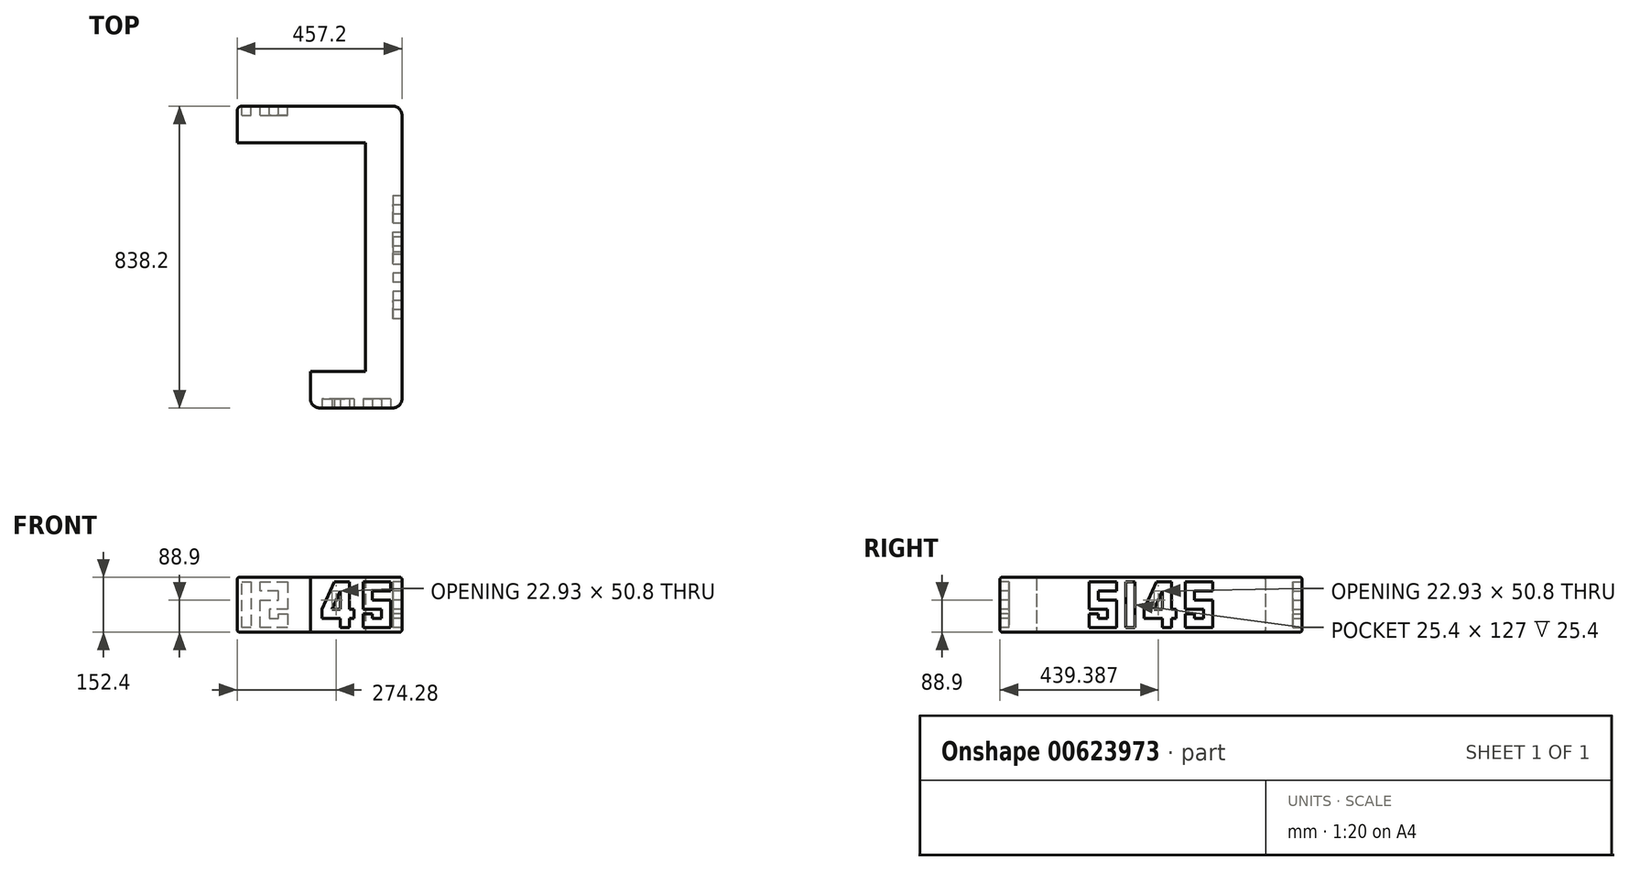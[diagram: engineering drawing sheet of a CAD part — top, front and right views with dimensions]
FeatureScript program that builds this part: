
annotation { "Feature Type Name" : "Feature", "Feature Type Description" : "" }
export const myFeature = defineFeature(function(context is Context, id is Id, definition is map)
    precondition{}
    {
        {
            var Q0;
            Q0=qCreatedBy(makeId("Top.planeOp"),FACE);
            var sketch = newSketch(context, id + "F0", { "sketchPlane" : qUnion([Q0])});
            skLineSegment(sketch, "E0", {"start": v(-261.38, 279.44) * mm, "end": v(94.22, 279.44) * mm});
            skLineSegment(sketch, "E1", {"start": v(94.22, 279.44) * mm, "end": v(94.22, -355.56) * mm});
            skLineSegment(sketch, "E2", {"start": v(94.22, -355.56) * mm, "end": v(-58.18, -355.56) * mm});
            skLineSegment(sketch, "E3", {"start": v(-58.18, -355.56) * mm, "end": v(-58.18, -457.16) * mm});
            skLineSegment(sketch, "E4", {"start": v(-58.18, -457.16) * mm, "end": v(195.82, -457.16) * mm});
            skLineSegment(sketch, "E5", {"start": v(195.82, -457.16) * mm, "end": v(195.82, 381.04) * mm});
            skLineSegment(sketch, "E6", {"start": v(195.82, 381.04) * mm, "end": v(-261.38, 381.04) * mm});
            skLineSegment(sketch, "E7", {"start": v(-261.38, 381.04) * mm, "end": v(-261.38, 279.44) * mm});
            skSolve(sketch);
        }
        {
            var Q0;
            Q0=makeQuery(id+"F0.imprint","IMPRINT",FACE,{"disambiguationData":[TD([[makeQuery(id+"F0.imprint","IMPRINT",EDGE,{"derivedFrom":sQuery(id+"F0.wireOp",EDGE,"E0")}),1.0]])]});
            extrude(context, id + "F1", {"entities" : qUnion([Q0]), "depth" : 152.4 * mm, "offsetDistance" : 25.4 * mm});
        }
        {
            var Q0;
            Q0=makeQuery(id+"F1.opExtrude","SWEPT_EDGE",EDGE,{"disambiguationData":[OSD([sQuery(id+"F0.wireOp",EDGE,"E4"),sQuery(id+"F0.wireOp",EDGE,"E5")])]});
            var Q1;
            Q1=makeQuery(id+"F1.opExtrude","SWEPT_EDGE",EDGE,{"disambiguationData":[OSD([sQuery(id+"F0.wireOp",EDGE,"E3"),sQuery(id+"F0.wireOp",EDGE,"E4")])]});
            var Q2;
            Q2=makeQuery(id+"F1.opExtrude","SWEPT_EDGE",EDGE,{"disambiguationData":[OSD([sQuery(id+"F0.wireOp",EDGE,"E5"),sQuery(id+"F0.wireOp",EDGE,"E6")])]});
            fillet(context, id + "F2", {"entities" : qUnion([Q0, Q1, Q2]), "radius" : 25.4 * mm, "tangentPropagation" : true, "allowEdgeOverflow" : false});
        }
        {
            var Q0;
            Q0=makeQuery(id+"F1.opExtrude","SWEPT_FACE",FACE,{"disambiguationData":[OSD([sQuery(id+"F0.wireOp",EDGE,"E5")])]});
            var sketch = newSketch(context, id + "F3", { "sketchPlane" : qUnion([Q0])});
            skLineSegment(sketch, "E8", {"start": v(-133.3, 139.7) * mm, "end": v(-209.5, 139.7) * mm});
            skLineSegment(sketch, "E9", {"start": v(-209.5, 139.7) * mm, "end": v(-209.5, 63.5) * mm});
            skLineSegment(sketch, "E10", {"start": v(-209.5, 63.5) * mm, "end": v(-158.7, 63.5) * mm});
            skLineSegment(sketch, "E11", {"start": v(-158.7, 63.5) * mm, "end": v(-158.7, 38.1) * mm});
            skLineSegment(sketch, "E12", {"start": v(-158.7, 38.1) * mm, "end": v(-184.1, 38.1) * mm});
            skLineSegment(sketch, "E13", {"start": v(-184.1, 38.1) * mm, "end": v(-184.1, 50.8) * mm});
            skLineSegment(sketch, "E14", {"start": v(-184.1, 50.8) * mm, "end": v(-209.5, 50.8) * mm});
            skLineSegment(sketch, "E15", {"start": v(-209.5, 50.8) * mm, "end": v(-209.5, 12.7) * mm});
            skLineSegment(sketch, "E16", {"start": v(-209.5, 12.7) * mm, "end": v(-133.3, 12.7) * mm});
            skLineSegment(sketch, "E17", {"start": v(-133.3, 12.7) * mm, "end": v(-133.3, 88.9) * mm});
            skLineSegment(sketch, "E18", {"start": v(-133.3, 88.9) * mm, "end": v(-184.1, 88.9) * mm});
            skLineSegment(sketch, "E19", {"start": v(-184.1, 88.9) * mm, "end": v(-184.1, 114.3) * mm});
            skLineSegment(sketch, "E20", {"start": v(-184.1, 114.3) * mm, "end": v(-133.3, 114.3) * mm});
            skLineSegment(sketch, "E21", {"start": v(-133.3, 114.3) * mm, "end": v(-133.3, 139.7) * mm});
            skLineSegment(sketch, "E22", {"start": v(-107.9, 139.7) * mm, "end": v(-107.9, 12.7) * mm});
            skLineSegment(sketch, "E23", {"start": v(-107.9, 12.7) * mm, "end": v(-82.5, 12.7) * mm});
            skLineSegment(sketch, "E24", {"start": v(-82.5, 12.7) * mm, "end": v(-82.5, 139.7) * mm});
            skLineSegment(sketch, "E25", {"start": v(-82.5, 139.7) * mm, "end": v(-107.9, 139.7) * mm});
            skLineSegment(sketch, "E26", {"start": v(19.1, 139.7) * mm, "end": v(-22.7, 139.7) * mm});
            skLineSegment(sketch, "E27", {"start": v(-22.7, 139.7) * mm, "end": v(-57.1, 63.5) * mm});
            skLineSegment(sketch, "E28", {"start": v(-57.1, 63.5) * mm, "end": v(-57.1, 38.1) * mm});
            skLineSegment(sketch, "E29", {"start": v(-57.1, 38.1) * mm, "end": v(-6.3, 38.1) * mm});
            skLineSegment(sketch, "E30", {"start": v(-6.3, 38.1) * mm, "end": v(-6.3, 12.7) * mm});
            skLineSegment(sketch, "E31", {"start": v(-6.3, 12.7) * mm, "end": v(19.1, 12.7) * mm});
            skLineSegment(sketch, "E32", {"start": v(19.1, 12.7) * mm, "end": v(19.1, 38.1) * mm});
            skLineSegment(sketch, "E33", {"start": v(19.1, 38.1) * mm, "end": v(31.8, 38.1) * mm});
            skLineSegment(sketch, "E34", {"start": v(31.8, 38.1) * mm, "end": v(31.8, 63.5) * mm});
            skLineSegment(sketch, "E35", {"start": v(31.8, 63.5) * mm, "end": v(19.1, 63.5) * mm});
            skLineSegment(sketch, "E36", {"start": v(19.1, 139.7) * mm, "end": v(19.1, 63.5) * mm});
            skLineSegment(sketch, "E37", {"start": v(-6.3, 63.5) * mm, "end": v(-29.24, 63.5) * mm});
            skLineSegment(sketch, "E38", {"start": v(-29.24, 63.5) * mm, "end": v(-6.3, 114.3) * mm});
            skLineSegment(sketch, "E39", {"start": v(-6.3, 114.3) * mm, "end": v(-6.3, 63.5) * mm});
            skLineSegment(sketch, "E40", {"start": v(133.4, 139.7) * mm, "end": v(57.2, 139.7) * mm});
            skLineSegment(sketch, "E41", {"start": v(57.2, 139.7) * mm, "end": v(57.2, 63.5) * mm});
            skLineSegment(sketch, "E42", {"start": v(57.2, 63.5) * mm, "end": v(108, 63.5) * mm});
            skLineSegment(sketch, "E43", {"start": v(108, 63.5) * mm, "end": v(108, 38.1) * mm});
            skLineSegment(sketch, "E44", {"start": v(108, 38.1) * mm, "end": v(82.6, 38.1) * mm});
            skLineSegment(sketch, "E45", {"start": v(82.6, 38.1) * mm, "end": v(82.6, 50.8) * mm});
            skLineSegment(sketch, "E46", {"start": v(82.6, 50.8) * mm, "end": v(57.2, 50.8) * mm});
            skLineSegment(sketch, "E47", {"start": v(57.2, 50.8) * mm, "end": v(57.2, 12.7) * mm});
            skLineSegment(sketch, "E48", {"start": v(57.2, 12.7) * mm, "end": v(133.4, 12.7) * mm});
            skLineSegment(sketch, "E49", {"start": v(133.4, 12.7) * mm, "end": v(133.4, 88.9) * mm});
            skLineSegment(sketch, "E50", {"start": v(133.4, 88.9) * mm, "end": v(82.6, 88.9) * mm});
            skLineSegment(sketch, "E51", {"start": v(82.6, 88.9) * mm, "end": v(82.6, 114.3) * mm});
            skLineSegment(sketch, "E52", {"start": v(82.6, 114.3) * mm, "end": v(133.4, 114.3) * mm});
            skLineSegment(sketch, "E53", {"start": v(133.4, 114.3) * mm, "end": v(133.4, 139.7) * mm});
            skLineSegment(sketch, "E54", {"start": v(-209.5, 139.7) * mm, "end": v(-431.76, 139.7) * mm});
            skLineSegment(sketch, "E55", {"start": v(133.4, 139.7) * mm, "end": v(355.64, 139.7) * mm});
            skSolve(sketch);
        }
        {
            var Q0;
            Q0=makeQuery(id+"F3.imprint","IMPRINT",FACE,{"disambiguationData":[TD([[makeQuery(id+"F3.imprint","IMPRINT",EDGE,{"derivedFrom":sQuery(id+"F3.wireOp",EDGE,"E8")}),1.0]])]});
            var Q1;
            Q1=makeQuery(id+"F3.imprint","IMPRINT",FACE,{"disambiguationData":[TD([[makeQuery(id+"F3.imprint","IMPRINT",EDGE,{"derivedFrom":sQuery(id+"F3.wireOp",EDGE,"E22")}),1.0]])]});
            var Q2;
            Q2=makeQuery(id+"F3.imprint","IMPRINT",FACE,{"disambiguationData":[TD([[makeQuery(id+"F3.imprint","IMPRINT",EDGE,{"derivedFrom":sQuery(id+"F3.wireOp",EDGE,"E26")}),1.0]])]});
            var Q3;
            Q3=makeQuery(id+"F3.imprint","IMPRINT",FACE,{"disambiguationData":[TD([[makeQuery(id+"F3.imprint","IMPRINT",EDGE,{"derivedFrom":sQuery(id+"F3.wireOp",EDGE,"E40")}),1.0]])]});
            extrude(context, id + "F4", {"entities" : qUnion([Q0, Q1, Q2, Q3]), "operationType" : NewBodyOperationType.REMOVE, "oppositeDirection" : true, "depth" : 25.4 * mm, "offsetDistance" : 25.4 * mm});
        }
        {
            var Q0;
            Q0=makeQuery(id+"F4.boolean.opBoolean","COPY",FACE,{"derivedFrom":makeQuery(id+"F4.opExtrude","CAP_FACE",FACE,{"disambiguationData":[OSD([sQuery(id+"F3.wireOp",EDGE,"E8"),sQuery(id+"F3.wireOp",EDGE,"E9"),sQuery(id+"F3.wireOp",EDGE,"E10"),sQuery(id+"F3.wireOp",EDGE,"E11"),sQuery(id+"F3.wireOp",EDGE,"E12"),sQuery(id+"F3.wireOp",EDGE,"E13"),sQuery(id+"F3.wireOp",EDGE,"E14"),sQuery(id+"F3.wireOp",EDGE,"E15"),sQuery(id+"F3.wireOp",EDGE,"E16"),sQuery(id+"F3.wireOp",EDGE,"E17"),sQuery(id+"F3.wireOp",EDGE,"E18"),sQuery(id+"F3.wireOp",EDGE,"E19"),sQuery(id+"F3.wireOp",EDGE,"E20"),sQuery(id+"F3.wireOp",EDGE,"E21")])],"isStart":false})});
            var Q1;
            Q1=makeQuery(id+"F4.boolean.opBoolean","COPY",FACE,{"derivedFrom":makeQuery(id+"F4.opExtrude","CAP_FACE",FACE,{"disambiguationData":[OSD([sQuery(id+"F3.wireOp",EDGE,"E22"),sQuery(id+"F3.wireOp",EDGE,"E23"),sQuery(id+"F3.wireOp",EDGE,"E24"),sQuery(id+"F3.wireOp",EDGE,"E25")])],"isStart":false})});
            var Q2;
            Q2=makeQuery(id+"F4.boolean.opBoolean","COPY",FACE,{"derivedFrom":makeQuery(id+"F4.opExtrude","CAP_FACE",FACE,{"disambiguationData":[OSD([sQuery(id+"F3.wireOp",EDGE,"E26"),sQuery(id+"F3.wireOp",EDGE,"E27"),sQuery(id+"F3.wireOp",EDGE,"E28"),sQuery(id+"F3.wireOp",EDGE,"E29"),sQuery(id+"F3.wireOp",EDGE,"E30"),sQuery(id+"F3.wireOp",EDGE,"E31"),sQuery(id+"F3.wireOp",EDGE,"E32"),sQuery(id+"F3.wireOp",EDGE,"E33"),sQuery(id+"F3.wireOp",EDGE,"E34"),sQuery(id+"F3.wireOp",EDGE,"E35"),sQuery(id+"F3.wireOp",EDGE,"E36"),sQuery(id+"F3.wireOp",EDGE,"E37"),sQuery(id+"F3.wireOp",EDGE,"E38"),sQuery(id+"F3.wireOp",EDGE,"E39")])],"isStart":false})});
            var Q3;
            Q3=makeQuery(id+"F4.boolean.opBoolean","COPY",FACE,{"derivedFrom":makeQuery(id+"F4.opExtrude","CAP_FACE",FACE,{"disambiguationData":[OSD([sQuery(id+"F3.wireOp",EDGE,"E40"),sQuery(id+"F3.wireOp",EDGE,"E41"),sQuery(id+"F3.wireOp",EDGE,"E42"),sQuery(id+"F3.wireOp",EDGE,"E43"),sQuery(id+"F3.wireOp",EDGE,"E44"),sQuery(id+"F3.wireOp",EDGE,"E45"),sQuery(id+"F3.wireOp",EDGE,"E46"),sQuery(id+"F3.wireOp",EDGE,"E47"),sQuery(id+"F3.wireOp",EDGE,"E48"),sQuery(id+"F3.wireOp",EDGE,"E49"),sQuery(id+"F3.wireOp",EDGE,"E50"),sQuery(id+"F3.wireOp",EDGE,"E51"),sQuery(id+"F3.wireOp",EDGE,"E52"),sQuery(id+"F3.wireOp",EDGE,"E53")])],"isStart":false})});
            extrude(context, id + "F5", {"entities" : qUnion([Q0, Q1, Q2, Q3]), "depth" : 25.4 * mm, "offsetDistance" : 25.4 * mm});
        }
        {
            var Q0;
            Q0=makeQuery(id+"F1.opExtrude","SWEPT_FACE",FACE,{"disambiguationData":[OSD([sQuery(id+"F0.wireOp",EDGE,"E4")])]});
            var sketch = newSketch(context, id + "F6", { "sketchPlane" : qUnion([Q0])});
            skLineSegment(sketch, "E56", {"start": v(7.96, 139.7) * mm, "end": v(49.77, 139.7) * mm});
            skLineSegment(sketch, "E57", {"start": v(49.77, 139.7) * mm, "end": v(49.77, 63.5) * mm});
            skLineSegment(sketch, "E58", {"start": v(49.77, 63.5) * mm, "end": v(62.47, 63.5) * mm});
            skLineSegment(sketch, "E59", {"start": v(62.47, 63.5) * mm, "end": v(62.47, 38.1) * mm});
            skLineSegment(sketch, "E60", {"start": v(62.47, 38.1) * mm, "end": v(49.77, 38.1) * mm});
            skLineSegment(sketch, "E61", {"start": v(49.77, 38.1) * mm, "end": v(49.77, 12.7) * mm});
            skLineSegment(sketch, "E62", {"start": v(49.77, 12.7) * mm, "end": v(24.37, 12.7) * mm});
            skLineSegment(sketch, "E63", {"start": v(24.37, 12.7) * mm, "end": v(24.37, 38.1) * mm});
            skLineSegment(sketch, "E64", {"start": v(24.37, 38.1) * mm, "end": v(-26.43, 38.1) * mm});
            skLineSegment(sketch, "E65", {"start": v(-26.43, 38.1) * mm, "end": v(-26.43, 63.5) * mm});
            skLineSegment(sketch, "E66", {"start": v(-26.43, 63.5) * mm, "end": v(7.96, 139.7) * mm});
            skLineSegment(sketch, "E67", {"start": v(24.37, 63.5) * mm, "end": v(1.43, 63.5) * mm});
            skLineSegment(sketch, "E68", {"start": v(1.43, 63.5) * mm, "end": v(24.37, 114.3) * mm});
            skLineSegment(sketch, "E69", {"start": v(24.37, 114.3) * mm, "end": v(24.37, 63.5) * mm});
            skLineSegment(sketch, "E70", {"start": v(164.07, 139.7) * mm, "end": v(87.87, 139.7) * mm});
            skLineSegment(sketch, "E71", {"start": v(87.87, 139.7) * mm, "end": v(87.87, 63.5) * mm});
            skLineSegment(sketch, "E72", {"start": v(87.87, 63.5) * mm, "end": v(138.67, 63.5) * mm});
            skLineSegment(sketch, "E73", {"start": v(138.67, 63.5) * mm, "end": v(138.67, 38.1) * mm});
            skLineSegment(sketch, "E74", {"start": v(138.67, 38.1) * mm, "end": v(113.27, 38.1) * mm});
            skLineSegment(sketch, "E75", {"start": v(113.27, 38.1) * mm, "end": v(113.27, 50.8) * mm});
            skLineSegment(sketch, "E76", {"start": v(113.27, 50.8) * mm, "end": v(87.87, 50.8) * mm});
            skLineSegment(sketch, "E77", {"start": v(87.87, 50.8) * mm, "end": v(87.87, 12.7) * mm});
            skLineSegment(sketch, "E78", {"start": v(87.87, 12.7) * mm, "end": v(164.07, 12.7) * mm});
            skLineSegment(sketch, "E79", {"start": v(164.07, 12.7) * mm, "end": v(164.07, 88.9) * mm});
            skLineSegment(sketch, "E80", {"start": v(164.07, 88.9) * mm, "end": v(113.27, 88.9) * mm});
            skLineSegment(sketch, "E81", {"start": v(113.27, 88.9) * mm, "end": v(113.27, 114.3) * mm});
            skLineSegment(sketch, "E82", {"start": v(113.27, 114.3) * mm, "end": v(164.07, 114.3) * mm});
            skLineSegment(sketch, "E83", {"start": v(164.07, 114.3) * mm, "end": v(164.07, 139.7) * mm});
            skSolve(sketch);
        }
        {
            var Q0;
            Q0=makeQuery(id+"F6.imprint","IMPRINT",FACE,{"disambiguationData":[TD([[makeQuery(id+"F6.imprint","IMPRINT",EDGE,{"derivedFrom":sQuery(id+"F6.wireOp",EDGE,"E56")}),-1.0]])]});
            var Q1;
            Q1=makeQuery(id+"F6.imprint","IMPRINT",FACE,{"disambiguationData":[TD([[makeQuery(id+"F6.imprint","IMPRINT",EDGE,{"derivedFrom":sQuery(id+"F6.wireOp",EDGE,"E70")}),1.0]])]});
            extrude(context, id + "F7", {"entities" : qUnion([Q0, Q1]), "operationType" : NewBodyOperationType.REMOVE, "oppositeDirection" : true, "depth" : 25.4 * mm, "offsetDistance" : 25.4 * mm});
        }
        {
            var Q0;
            Q0=makeQuery(id+"F7.boolean.opBoolean","COPY",FACE,{"derivedFrom":makeQuery(id+"F7.opExtrude","CAP_FACE",FACE,{"disambiguationData":[OSD([sQuery(id+"F6.wireOp",EDGE,"E56"),sQuery(id+"F6.wireOp",EDGE,"E57"),sQuery(id+"F6.wireOp",EDGE,"E58"),sQuery(id+"F6.wireOp",EDGE,"E59"),sQuery(id+"F6.wireOp",EDGE,"E60"),sQuery(id+"F6.wireOp",EDGE,"E61"),sQuery(id+"F6.wireOp",EDGE,"E62"),sQuery(id+"F6.wireOp",EDGE,"E63"),sQuery(id+"F6.wireOp",EDGE,"E64"),sQuery(id+"F6.wireOp",EDGE,"E65"),sQuery(id+"F6.wireOp",EDGE,"E66"),sQuery(id+"F6.wireOp",EDGE,"E67"),sQuery(id+"F6.wireOp",EDGE,"E68"),sQuery(id+"F6.wireOp",EDGE,"E69")])],"isStart":false})});
            var Q1;
            Q1=makeQuery(id+"F7.boolean.opBoolean","COPY",FACE,{"derivedFrom":makeQuery(id+"F7.opExtrude","CAP_FACE",FACE,{"disambiguationData":[OSD([sQuery(id+"F6.wireOp",EDGE,"E70"),sQuery(id+"F6.wireOp",EDGE,"E71"),sQuery(id+"F6.wireOp",EDGE,"E72"),sQuery(id+"F6.wireOp",EDGE,"E73"),sQuery(id+"F6.wireOp",EDGE,"E74"),sQuery(id+"F6.wireOp",EDGE,"E75"),sQuery(id+"F6.wireOp",EDGE,"E76"),sQuery(id+"F6.wireOp",EDGE,"E77"),sQuery(id+"F6.wireOp",EDGE,"E78"),sQuery(id+"F6.wireOp",EDGE,"E79"),sQuery(id+"F6.wireOp",EDGE,"E80"),sQuery(id+"F6.wireOp",EDGE,"E81"),sQuery(id+"F6.wireOp",EDGE,"E82"),sQuery(id+"F6.wireOp",EDGE,"E83")])],"isStart":false})});
            extrude(context, id + "F8", {"entities" : qUnion([Q0, Q1]), "depth" : 25.4 * mm, "offsetDistance" : 25.4 * mm});
        }
        {
            var Q0;
            Q0=makeQuery(id+"F1.opExtrude","SWEPT_FACE",FACE,{"disambiguationData":[OSD([sQuery(id+"F0.wireOp",EDGE,"E6")])]});
            var sketch = newSketch(context, id + "F9", { "sketchPlane" : qUnion([Q0])});
            skLineSegment(sketch, "E84", {"start": v(248.68, 139.7) * mm, "end": v(223.28, 139.7) * mm});
            skLineSegment(sketch, "E85", {"start": v(223.28, 139.7) * mm, "end": v(223.28, 12.7) * mm});
            skLineSegment(sketch, "E86", {"start": v(223.28, 12.7) * mm, "end": v(248.68, 12.7) * mm});
            skLineSegment(sketch, "E87", {"start": v(248.68, 12.7) * mm, "end": v(248.68, 139.7) * mm});
            skLineSegment(sketch, "E88", {"start": v(197.88, 139.7) * mm, "end": v(121.68, 139.7) * mm});
            skLineSegment(sketch, "E89", {"start": v(121.68, 139.7) * mm, "end": v(121.68, 63.5) * mm});
            skLineSegment(sketch, "E90", {"start": v(121.68, 63.5) * mm, "end": v(172.48, 63.5) * mm});
            skLineSegment(sketch, "E91", {"start": v(172.48, 63.5) * mm, "end": v(172.48, 38.1) * mm});
            skLineSegment(sketch, "E92", {"start": v(172.48, 38.1) * mm, "end": v(147.08, 38.1) * mm});
            skLineSegment(sketch, "E93", {"start": v(147.08, 38.1) * mm, "end": v(147.08, 50.8) * mm});
            skLineSegment(sketch, "E94", {"start": v(147.08, 50.8) * mm, "end": v(121.68, 50.8) * mm});
            skLineSegment(sketch, "E95", {"start": v(121.68, 50.8) * mm, "end": v(121.68, 12.7) * mm});
            skLineSegment(sketch, "E96", {"start": v(121.68, 12.7) * mm, "end": v(197.88, 12.7) * mm});
            skLineSegment(sketch, "E97", {"start": v(197.88, 12.7) * mm, "end": v(197.88, 88.9) * mm});
            skLineSegment(sketch, "E98", {"start": v(197.88, 88.9) * mm, "end": v(147.08, 88.9) * mm});
            skLineSegment(sketch, "E99", {"start": v(147.08, 88.9) * mm, "end": v(147.08, 114.3) * mm});
            skLineSegment(sketch, "E100", {"start": v(147.08, 114.3) * mm, "end": v(197.88, 114.3) * mm});
            skLineSegment(sketch, "E101", {"start": v(197.88, 114.3) * mm, "end": v(197.88, 139.7) * mm});
            skSolve(sketch);
        }
        {
            var Q0;
            Q0=makeQuery(id+"F9.imprint","IMPRINT",FACE,{"disambiguationData":[TD([[makeQuery(id+"F9.imprint","IMPRINT",EDGE,{"derivedFrom":sQuery(id+"F9.wireOp",EDGE,"E88")}),1.0]])]});
            var Q1;
            Q1=makeQuery(id+"F9.imprint","IMPRINT",FACE,{"disambiguationData":[TD([[makeQuery(id+"F9.imprint","IMPRINT",EDGE,{"derivedFrom":sQuery(id+"F9.wireOp",EDGE,"E84")}),1.0]])]});
            extrude(context, id + "F10", {"entities" : qUnion([Q0, Q1]), "operationType" : NewBodyOperationType.REMOVE, "oppositeDirection" : true, "depth" : 25.4 * mm, "offsetDistance" : 25.4 * mm});
        }
        {
            var Q0;
            Q0=makeQuery(id+"F10.boolean.opBoolean","COPY",FACE,{"derivedFrom":makeQuery(id+"F10.opExtrude","CAP_FACE",FACE,{"disambiguationData":[OSD([sQuery(id+"F9.wireOp",EDGE,"E88"),sQuery(id+"F9.wireOp",EDGE,"E89"),sQuery(id+"F9.wireOp",EDGE,"E90"),sQuery(id+"F9.wireOp",EDGE,"E91"),sQuery(id+"F9.wireOp",EDGE,"E92"),sQuery(id+"F9.wireOp",EDGE,"E93"),sQuery(id+"F9.wireOp",EDGE,"E94"),sQuery(id+"F9.wireOp",EDGE,"E95"),sQuery(id+"F9.wireOp",EDGE,"E96"),sQuery(id+"F9.wireOp",EDGE,"E97"),sQuery(id+"F9.wireOp",EDGE,"E98"),sQuery(id+"F9.wireOp",EDGE,"E99"),sQuery(id+"F9.wireOp",EDGE,"E100"),sQuery(id+"F9.wireOp",EDGE,"E101")])],"isStart":false})});
            var Q1;
            Q1=makeQuery(id+"F10.boolean.opBoolean","COPY",FACE,{"derivedFrom":makeQuery(id+"F10.opExtrude","CAP_FACE",FACE,{"disambiguationData":[OSD([sQuery(id+"F9.wireOp",EDGE,"E84"),sQuery(id+"F9.wireOp",EDGE,"E85"),sQuery(id+"F9.wireOp",EDGE,"E86"),sQuery(id+"F9.wireOp",EDGE,"E87")])],"isStart":false})});
            extrude(context, id + "F11", {"entities" : qUnion([Q0, Q1]), "depth" : 25.4 * mm, "offsetDistance" : 25.4 * mm});
        }
        {
            var Q0;
            Q0=makeQuery(id+"F1.opExtrude","SWEPT_EDGE",EDGE,{"disambiguationData":[OSD([sQuery(id+"F0.wireOp",EDGE,"E6"),sQuery(id+"F0.wireOp",EDGE,"E7")])]});
            fillet(context, id + "F12", {"entities" : qUnion([Q0]), "radius" : 12.7 * mm, "tangentPropagation" : true, "allowEdgeOverflow" : false});
        }
        {
            var Q0;
            Q0=makeQuery(id+"F1.opExtrude","CAP_EDGE",EDGE,{"disambiguationData":[OSD([sQuery(id+"F0.wireOp",EDGE,"E5")])],"isStart":false});
            var Q1;
            Q1=makeQuery(id+"F1.opExtrude","CAP_EDGE",EDGE,{"disambiguationData":[OSD([sQuery(id+"F0.wireOp",EDGE,"E5")])],"isStart":true});
            fillet(context, id + "F13", {"entities" : qUnion([Q0, Q1]), "radius" : 6.35 * mm, "tangentPropagation" : true, "allowEdgeOverflow" : false});
        }
    });
